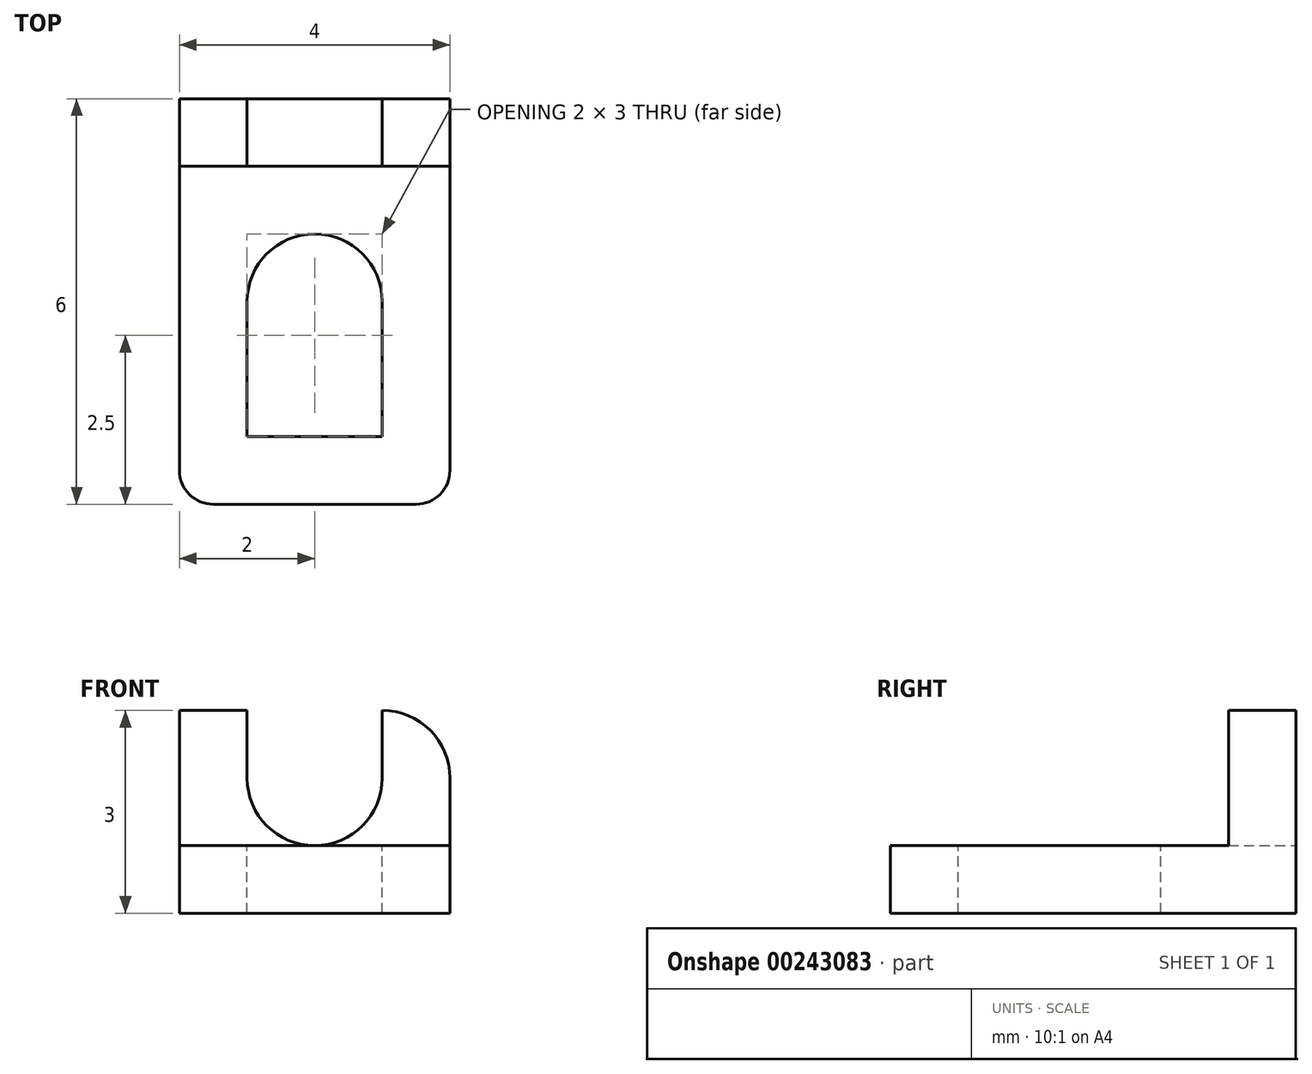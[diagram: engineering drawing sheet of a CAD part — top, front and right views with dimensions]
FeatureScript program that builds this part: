
annotation { "Feature Type Name" : "Feature", "Feature Type Description" : "" }
export const myFeature = defineFeature(function(context is Context, id is Id, definition is map)
    precondition{}
    {
        {
            var Q0;
            Q0=qCreatedBy(makeId("Top.planeOp"),FACE);
            var sketch = newSketch(context, id + "F0", { "sketchPlane" : qUnion([Q0])});
            skLineSegment(sketch, "E0", {"start": v(0, 0.5) * mm, "end": v(0, 6) * mm});
            skLineSegment(sketch, "E1", {"start": v(4, 6) * mm, "end": v(0, 6) * mm});
            skArc(sketch, "E2", {"start": v(0, 0.5) * mm, "mid": v(0.15, 0.15) * mm, "end": v(0.5, 0) * mm});
            skArc(sketch, "E3.MirrorCS", {"start": v(4, 0.5) * mm, "mid": v(3.85, 0.15) * mm, "end": v(3.5, 0) * mm});
            skLineSegment(sketch, "E4", {"start": v(0.5, 0) * mm, "end": v(3.5, 0) * mm});
            skLineSegment(sketch, "E5", {"start": v(4, 0.5) * mm, "end": v(4, 6) * mm});
            skSolve(sketch);
        }
        {
            var Q0;
            Q0 = qSketchRegion(id + "F0", true);
            extrude(context, id + "F1", {"entities" : qUnion([Q0]), "depth" : 1 * mm});
        }
        {
            var Q0;
            Q0=makeQuery(id+"F1.opExtrude","CAP_FACE",FACE,{"disambiguationData":[OSD([sQuery(id+"F0.wireOp",EDGE,"E0"),sQuery(id+"F0.wireOp",EDGE,"E1"),sQuery(id+"F0.wireOp",EDGE,"E2"),sQuery(id+"F0.wireOp",EDGE,"E3.MirrorCS"),sQuery(id+"F0.wireOp",EDGE,"E4"),sQuery(id+"F0.wireOp",EDGE,"E5")])],"isStart":false});
            var sketch = newSketch(context, id + "F2", { "sketchPlane" : qUnion([Q0])});
            skLineSegment(sketch, "E6", {"start": v(0, 0) * mm, "end": v(1, 0) * mm});
            skLineSegment(sketch, "E7", {"start": v(1, 0) * mm, "end": v(1, 1) * mm});
            skLineSegment(sketch, "E8", {"start": v(1, 1) * mm, "end": v(3, 1) * mm});
            skLineSegment(sketch, "E9", {"start": v(3, 1) * mm, "end": v(3, 3) * mm});
            skLineSegment(sketch, "E10", {"start": v(1, 1) * mm, "end": v(1, 3) * mm});
            skArc(sketch, "E11", {"start": v(3, 3) * mm, "mid": v(2, 4) * mm, "end": v(1, 3) * mm});
            skSolve(sketch);
        }
        {
            var Q0;
            Q0 = qSketchRegion(id + "F2", true);
            extrude(context, id + "F3", {"entities" : qUnion([Q0]), "operationType" : NewBodyOperationType.REMOVE, "oppositeDirection" : true, "depth" : 1 * mm});
        }
        {
            var Q0;
            Q0=makeQuery(id+"F1.opExtrude","SWEPT_FACE",FACE,{"disambiguationData":[OSD([sQuery(id+"F0.wireOp",EDGE,"E1")])]});
            var sketch = newSketch(context, id + "F4", { "sketchPlane" : qUnion([Q0])});
            skLineSegment(sketch, "E12", {"start": v(0, 1) * mm, "end": v(0, 3) * mm});
            skLineSegment(sketch, "E13", {"start": v(0, 3) * mm, "end": v(-1, 3) * mm});
            skLineSegment(sketch, "E14", {"start": v(-1, 3) * mm, "end": v(-1, 2) * mm});
            skArc(sketch, "E15", {"start": v(-3, 2) * mm, "mid": v(-2, 1) * mm, "end": v(-1, 2) * mm});
            skLineSegment(sketch, "E16", {"start": v(-3, 2) * mm, "end": v(-3, 3) * mm});
            skLineSegment(sketch, "E17", {"start": v(-4, 1) * mm, "end": v(-4, 2) * mm});
            skArc(sketch, "E18", {"start": v(-3, 3) * mm, "mid": v(-3.7, 2.7) * mm, "end": v(-4, 2) * mm});
            skLineSegment(sketch, "E19", {"start": v(0, 1) * mm, "end": v(-4, 1) * mm});
            skSolve(sketch);
        }
        {
            var Q0;
            Q0 = qSketchRegion(id + "F4", true);
            extrude(context, id + "F5", {"entities" : qUnion([Q0]), "operationType" : NewBodyOperationType.ADD, "oppositeDirection" : true, "depth" : 1 * mm});
        }
    });
